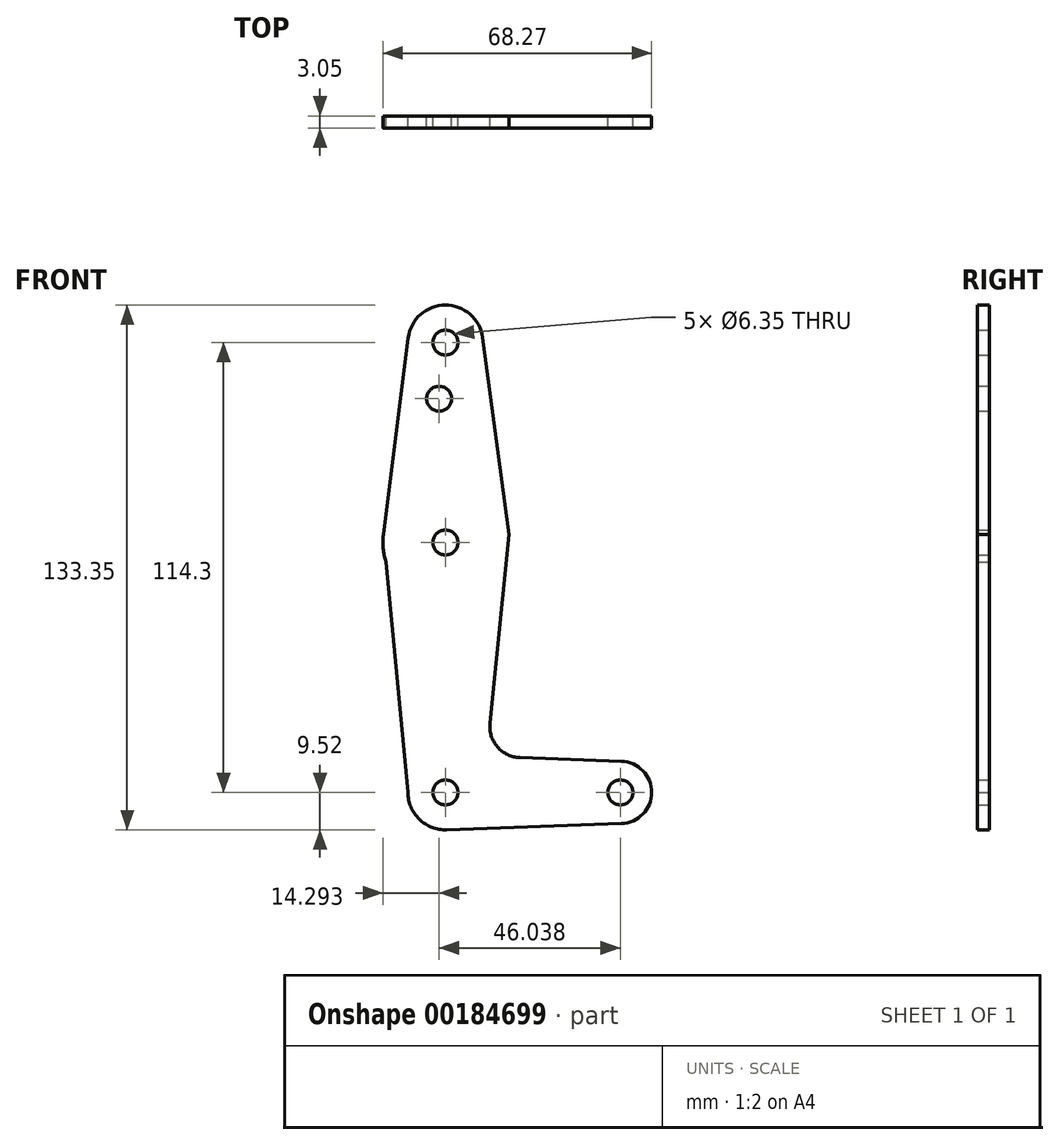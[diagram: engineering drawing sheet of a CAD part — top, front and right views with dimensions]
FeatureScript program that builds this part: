
annotation { "Feature Type Name" : "Feature", "Feature Type Description" : "" }
export const myFeature = defineFeature(function(context is Context, id is Id, definition is map)
    precondition{}
    {
        {
            var Q0;
            Q0=qCreatedBy(makeId("Front.planeOp"),FACE);
            var sketch = newSketch(context, id + "F0", { "sketchPlane" : qUnion([Q0])});
            skCircle(sketch, "E0", {"center": v(0, 0) * mm, "radius": 9.53 * mm});
            skCircle(sketch, "E1", {"center": v(44.45, 0) * mm, "radius": 7.94 * mm});
            skCircle(sketch, "E2", {"center": v(0, 63.5) * mm, "radius": 15.88 * mm});
            skCircle(sketch, "E3", {"center": v(0, 114.3) * mm, "radius": 9.53 * mm});
            skLineSegment(sketch, "E4", {"start": v(-9.52, 0) * mm, "end": v(-15.75, 65.48) * mm});
            skLineSegment(sketch, "E5", {"start": v(-9.45, 115.5) * mm, "end": v(-15.75, 65.48) * mm});
            skLineSegment(sketch, "E6", {"start": v(11.3, 17.6) * mm, "end": v(16.16, 65.48) * mm});
            skLineSegment(sketch, "E7", {"start": v(16.16, 65.48) * mm, "end": v(9.44, 115.57) * mm});
            skLineSegment(sketch, "E8", {"start": v(44.73, -7.93) * mm, "end": v(0, -9.53) * mm});
            skLineSegment(sketch, "E9", {"start": v(18.93, 8.85) * mm, "end": v(44.73, 7.93) * mm});
            skCircle(sketch, "E10", {"center": v(0, 114.3) * mm, "radius": 3.18 * mm});
            skCircle(sketch, "E11", {"center": v(0, 63.5) * mm, "radius": 3.18 * mm});
            skCircle(sketch, "E12", {"center": v(0, 0) * mm, "radius": 3.18 * mm});
            skCircle(sketch, "E13", {"center": v(44.45, 0) * mm, "radius": 3.18 * mm});
            skCircle(sketch, "E14", {"center": v(-1.59, 100.03) * mm, "radius": 3.18 * mm});
            skPoint(sketch, "E15.newPointB", {"position": v(0, 9.53) * mm});
            skArc(sketch, "E15.filletArc", {"start": v(11.3, 17.6) * mm, "mid": v(13.22, 11.57) * mm, "end": v(18.93, 8.85) * mm});
            skSolve(sketch);
        }
        {
            var Q0;
            Q0 = qSketchRegion(id + "F0", true);
            extrude(context, id + "F1", {"entities" : qUnion([Q0]), "depth" : 3.05 * mm});
        }
    });
